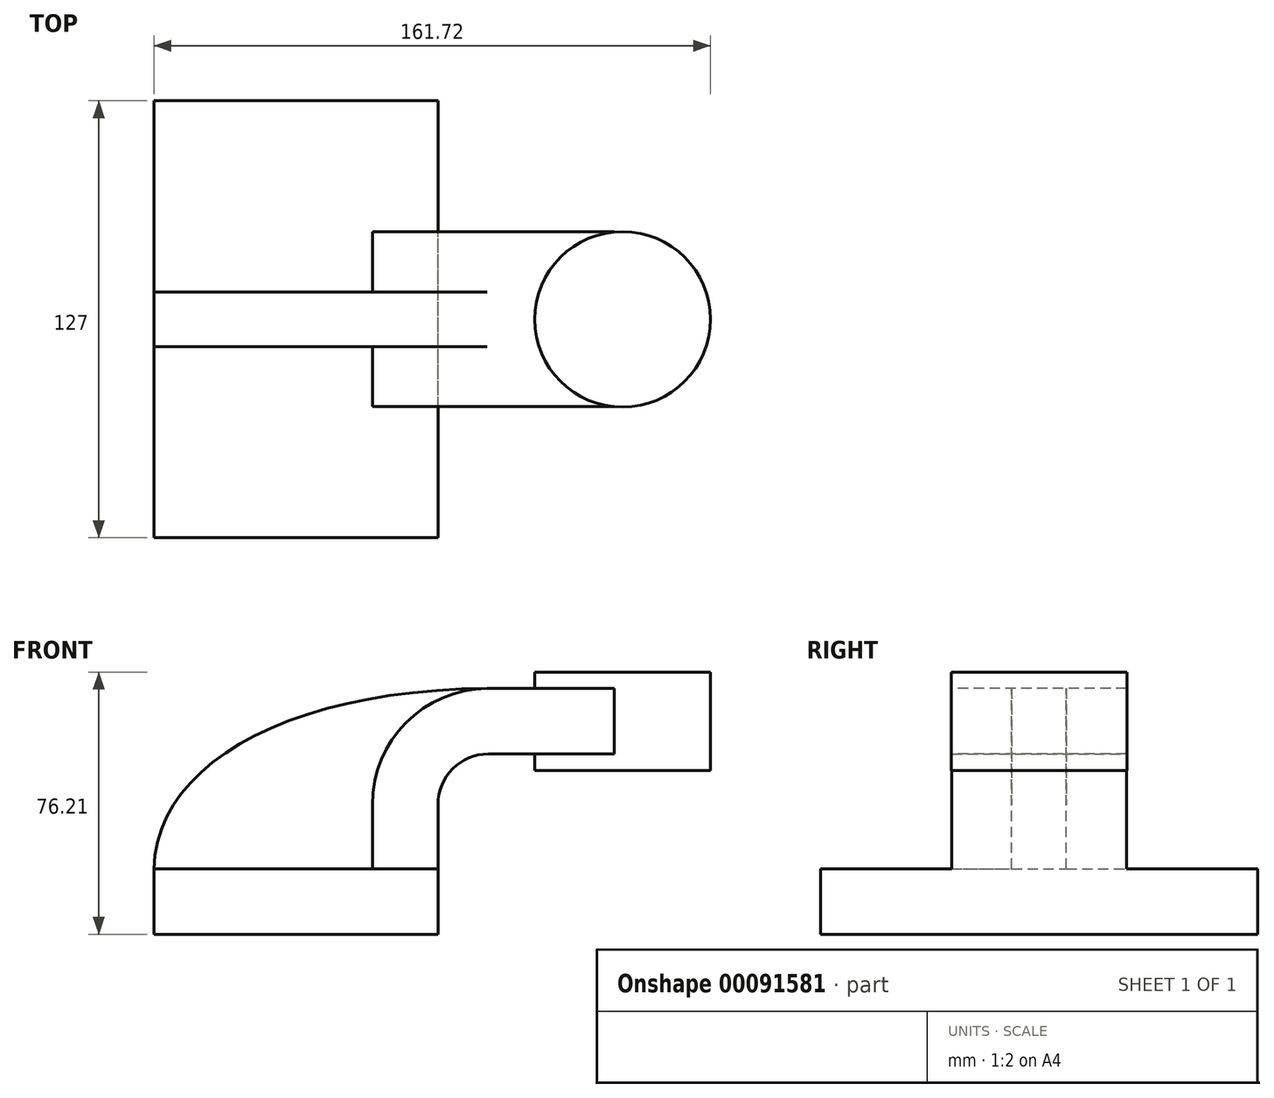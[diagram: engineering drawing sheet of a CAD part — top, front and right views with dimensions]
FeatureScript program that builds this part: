
annotation { "Feature Type Name" : "Feature", "Feature Type Description" : "" }
export const myFeature = defineFeature(function(context is Context, id is Id, definition is map)
    precondition{}
    {
        {
            var Q0;
            Q0=qCreatedBy(makeId("Front.planeOp"),FACE);
            var sketch = newSketch(context, id + "F0", { "sketchPlane" : qUnion([Q0])});
            skLineSegment(sketch, "E0.bottom", {"start": v(41.28, -9.52) * mm, "end": v(-41.28, -9.53) * mm});
            skLineSegment(sketch, "E0.top", {"start": v(41.27, 9.53) * mm, "end": v(-41.28, 9.53) * mm});
            skLineSegment(sketch, "E0.left", {"start": v(41.28, -9.52) * mm, "end": v(41.28, 9.53) * mm});
            skLineSegment(sketch, "E0.right", {"start": v(-41.28, -9.52) * mm, "end": v(-41.28, 9.53) * mm});
            skPoint(sketch, "E0.middle", {"position": v(0, 0) * mm});
            skLineSegment(sketch, "E1.bottom", {"start": v(120.44, 38.1) * mm, "end": v(69.64, 38.1) * mm});
            skLineSegment(sketch, "E1.top", {"start": v(120.44, 66.68) * mm, "end": v(69.64, 66.68) * mm});
            skLineSegment(sketch, "E1.left", {"start": v(120.44, 38.1) * mm, "end": v(120.44, 66.68) * mm});
            skLineSegment(sketch, "E1.right", {"start": v(69.64, 38.1) * mm, "end": v(69.64, 66.68) * mm});
            skPoint(sketch, "E1.middle", {"position": v(95.04, 52.39) * mm});
            skLineSegment(sketch, "E2", {"start": v(41.27, 9.53) * mm, "end": v(41.27, 28.2) * mm});
            skArc(sketch, "E3", {"start": v(41.27, 28.2) * mm, "mid": v(45.57, 38.58) * mm, "end": v(55.95, 42.88) * mm});
            skLineSegment(sketch, "E4", {"start": v(55.95, 42.88) * mm, "end": v(94.93, 42.88) * mm});
            skLineSegment(sketch, "E5.0", {"start": v(55.95, 61.93) * mm, "end": v(94.93, 61.93) * mm});
            skArc(sketch, "E5.1", {"start": v(22.22, 28.2) * mm, "mid": v(32.1, 52.05) * mm, "end": v(55.95, 61.93) * mm});
            skLineSegment(sketch, "E5.2", {"start": v(22.22, 9.53) * mm, "end": v(22.22, 28.2) * mm});
            skFitSpline(sketch, "E6", {"points": [v(-41.28, 9.53) * mm, v(55.95, 61.93) * mm], "startDerivative": vector(1.98, 91.61) * mm, "endDerivative": vector(172.62, 0.93) * mm});
            skLineSegment(sketch, "E7", {"start": v(94.93, 66.68) * mm, "end": v(94.93, 38.1) * mm});
            skSolve(sketch);
        }
        {
            var Q0;
            Q0=makeQuery(id+"F0.imprint","IMPRINT",FACE,{"disambiguationData":[TD([[makeQuery(id+"F0.imprint","IMPRINT",EDGE,{"derivedFrom":sQuery(id+"F0.wireOp",EDGE,"E0.bottom")}),-1.0]])]});
            extrude(context, id + "F1", {"entities" : qUnion([Q0]), "endBound" : BoundingType.SYMMETRIC, "depth" : 127 * mm});
        }
        {
            var Q0;
            {var subQ1=sQuery(id+"F0.wireOp",EDGE,"E2");Q0=makeQuery(id+"F0.imprint","IMPRINT",FACE,{"disambiguationData":[TD([[makeQuery(id+"F0.imprint","IMPRINT",EDGE,{"derivedFrom":subQ1}),1.0]])]});}
            var Q1;
            {var subQ0=sQuery(id+"F0.wireOp",EDGE,"E4");var subQ1=sQuery(id+"F0.wireOp",EDGE,"E1.right");var subQ2=makeQuery(id+"F0.imprint","INTERSECT",VERTEX,{"derivedFrom":[subQ1,subQ0]});Q1=makeQuery(id+"F0.imprint","IMPRINT",FACE,{"disambiguationData":[TD([[makeQuery(id+"F0.imprint","IMPRINT",EDGE,{"disambiguationData":[TD([[subQ2,-1.0]])],"derivedFrom":subQ1}),-1.0]])]});}
            extrude(context, id + "F2", {"entities" : qUnion([Q0, Q1]), "operationType" : NewBodyOperationType.ADD, "endBound" : BoundingType.SYMMETRIC, "depth" : 50.8 * mm});
        }
        {
            var Q0;
            {var subQ3=sQuery(id+"F0.wireOp",EDGE,"E5.2");Q0=makeQuery(id+"F0.imprint","IMPRINT",FACE,{"disambiguationData":[TD([[makeQuery(id+"F0.imprint","IMPRINT",EDGE,{"derivedFrom":subQ3}),1.0]])]});}
            extrude(context, id + "F3", {"entities" : qUnion([Q0]), "operationType" : NewBodyOperationType.ADD, "endBound" : BoundingType.SYMMETRIC, "depth" : 15.88 * mm});
        }
        {
            var Q0;
            {var subQ4=sQuery(id+"F0.wireOp",EDGE,"E1.left");Q0=makeQuery(id+"F0.imprint","IMPRINT",FACE,{"disambiguationData":[TD([[makeQuery(id+"F0.imprint","IMPRINT",EDGE,{"derivedFrom":subQ4}),1.0]])]});}
            var Q1;
            Q1=sQuery(id+"F0.wireOp",EDGE,"E7");
            revolve(context, id + "F4", {"operationType" : NewBodyOperationType.ADD, "entities" : qUnion([Q0]), "axis" : qUnion([Q1]), "revolveType" : RevolveType.FULL});
        }
    });
